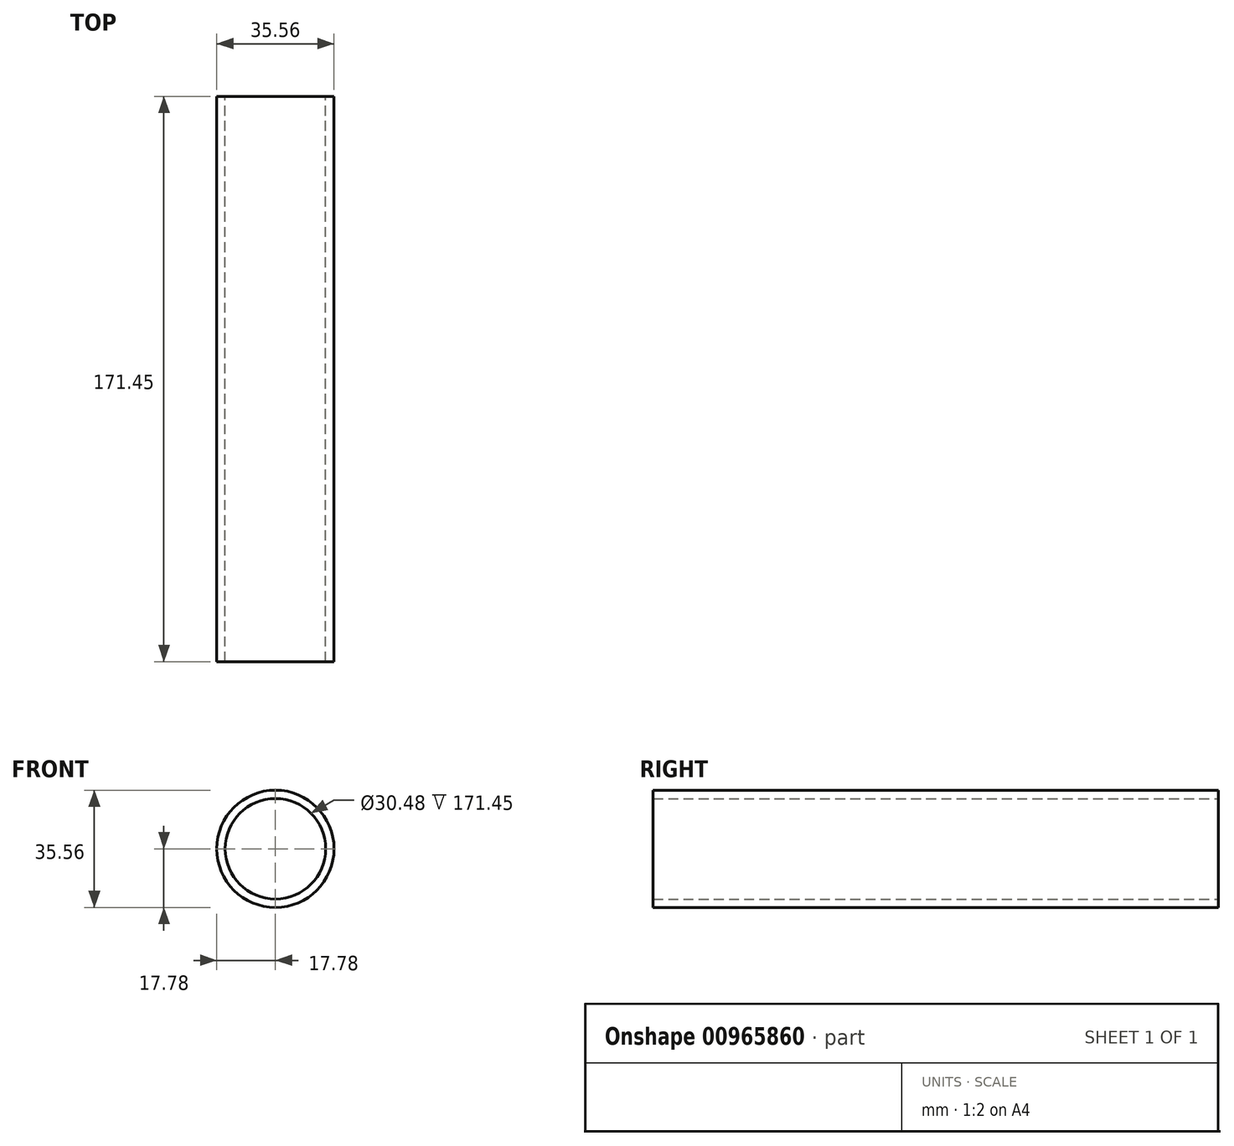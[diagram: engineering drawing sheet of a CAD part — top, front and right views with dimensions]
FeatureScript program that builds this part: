
annotation { "Feature Type Name" : "Feature", "Feature Type Description" : "" }
export const myFeature = defineFeature(function(context is Context, id is Id, definition is map)
    precondition{}
    {
        {
            var Q0;
            Q0=qCreatedBy(makeId("Front.planeOp"),FACE);
            var sketch = newSketch(context, id + "F0", { "sketchPlane" : qUnion([Q0])});
            skCircle(sketch, "E0", {"center": v(0, 0) * mm, "radius": 17.78 * mm});
            skCircle(sketch, "E1", {"center": v(0, 0) * mm, "radius": 15.24 * mm});
            skSolve(sketch);
        }
        {
            var Q0;
            Q0 = qSketchRegion(id + "F0", true);
            extrude(context, id + "F1", {"entities" : qUnion([Q0]), "depth" : 171.45 * mm, "offsetDistance" : 25.4 * mm});
        }
    });
